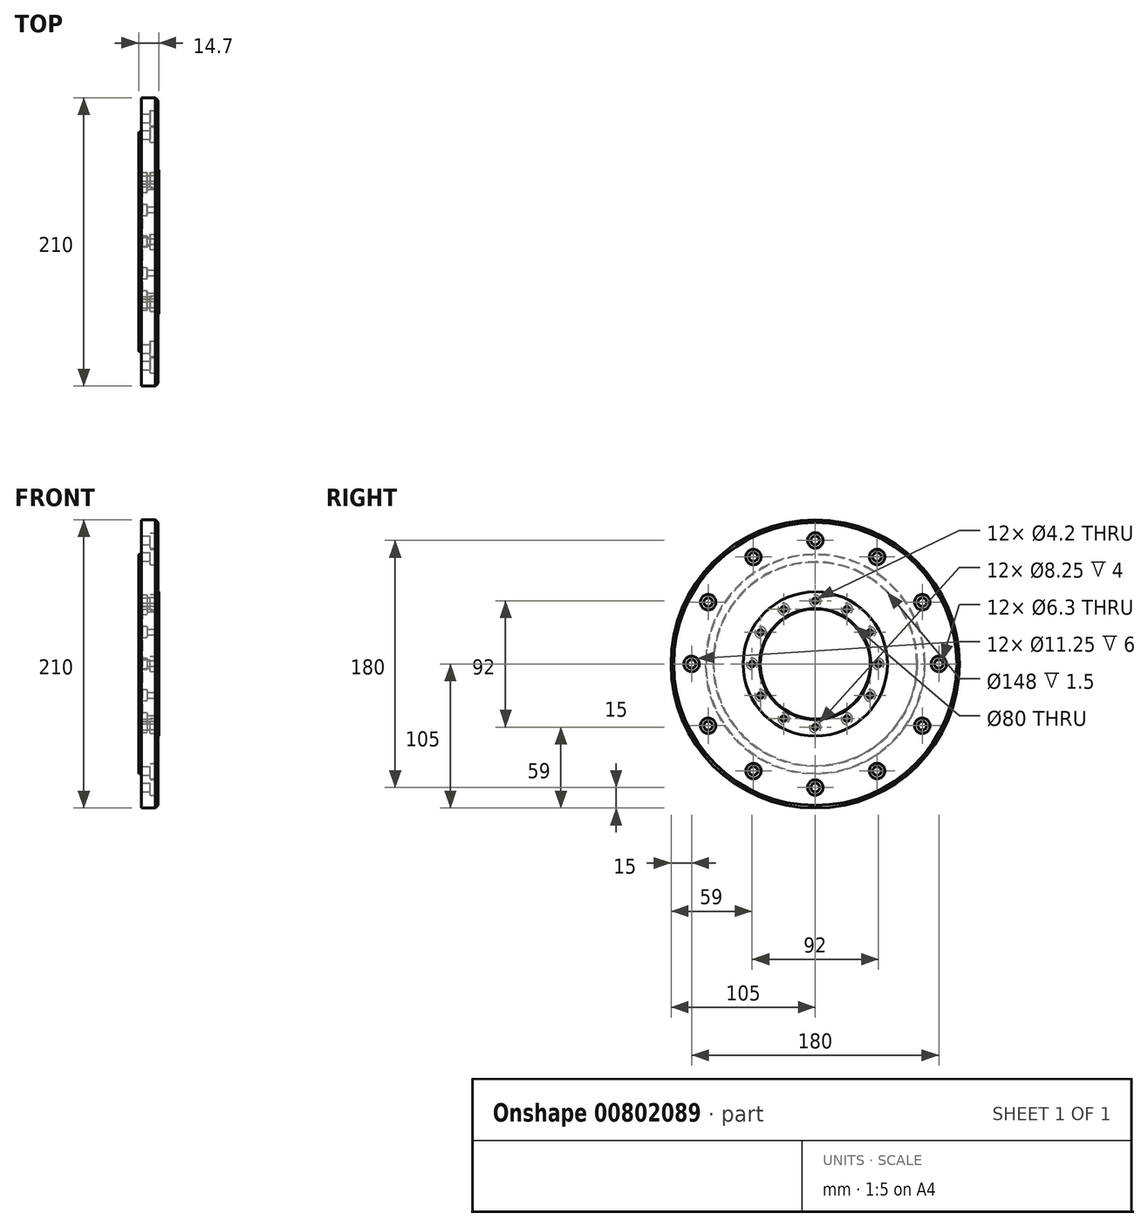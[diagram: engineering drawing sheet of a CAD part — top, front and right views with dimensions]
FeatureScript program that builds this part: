
annotation { "Feature Type Name" : "Feature", "Feature Type Description" : "" }
export const myFeature = defineFeature(function(context is Context, id is Id, definition is map)
    precondition{}
    {
        {
            var Q0;
            Q0=qCreatedBy(makeId("Front.planeOp"),FACE);
            var sketch = newSketch(context, id + "F0", { "sketchPlane" : qUnion([Q0])});
            skLineSegment(sketch, "E0", {"start": v(91.08, 0) * mm, "end": v(-135.26, 0) * mm, "construction": true});
            skLineSegment(sketch, "E1", {"start": v(-4.62, 80) * mm, "end": v(-4.62, 105) * mm});
            skLineSegment(sketch, "E2", {"start": v(-4.62, 105) * mm, "end": v(7.58, 105) * mm});
            skLineSegment(sketch, "E3", {"start": v(7.58, 105) * mm, "end": v(7.58, 52.5) * mm});
            skLineSegment(sketch, "E4", {"start": v(7.58, 52.5) * mm, "end": v(8.08, 52.5) * mm});
            skLineSegment(sketch, "E5", {"start": v(8.08, 52.5) * mm, "end": v(8.08, 40) * mm});
            skLineSegment(sketch, "E6", {"start": v(-4.62, 80) * mm, "end": v(-6.62, 80) * mm});
            skLineSegment(sketch, "E7", {"start": v(8.08, 40) * mm, "end": v(-4.62, 40) * mm});
            skLineSegment(sketch, "E8", {"start": v(-6.62, 80) * mm, "end": v(-6.62, 74) * mm});
            skLineSegment(sketch, "E9", {"start": v(-6.62, 74) * mm, "end": v(-4.62, 74) * mm});
            skLineSegment(sketch, "E10", {"start": v(-4.62, 74) * mm, "end": v(-4.62, 40) * mm});
            skPoint(sketch, "E11.orphan", {"position": v(-6.62, 40) * mm});
            skSolve(sketch);
        }
        {
            var Q0;
            Q0 = qSketchRegion(id + "F0", true);
            var Q1;
            Q1=sQuery(id+"F0.wireOp",EDGE,"E0");
            revolve(context, id + "F1", {"entities" : qUnion([Q0]), "axis" : qUnion([Q1]), "revolveType" : RevolveType.FULL});
        }
        {
            var Q0;
            Q0=makeQuery(id+"F1.opRevolve","SWEPT_FACE",FACE,{"disambiguationData":[OSD([sQuery(id+"F0.wireOp",EDGE,"E1")])]});
            var sketch = newSketch(context, id + "F2", { "sketchPlane" : qUnion([Q0])});
            skPoint(sketch, "E12", {"position": v(0, 0) * mm});
            skPoint(sketch, "E13", {"position": v(0, 46) * mm});
            skPoint(sketch, "E14", {"position": v(23, 39.84) * mm});
            skPoint(sketch, "E15", {"position": v(39.84, 23) * mm});
            skPoint(sketch, "E16", {"position": v(46, 0) * mm});
            skPoint(sketch, "E17", {"position": v(39.84, -23) * mm});
            skPoint(sketch, "E18", {"position": v(23, -39.84) * mm});
            skPoint(sketch, "E19", {"position": v(0, -46) * mm});
            skPoint(sketch, "E20", {"position": v(-23, -39.84) * mm});
            skPoint(sketch, "E21", {"position": v(-39.84, -23) * mm});
            skPoint(sketch, "E22", {"position": v(-46, 0) * mm});
            skPoint(sketch, "E23", {"position": v(-39.84, 23) * mm});
            skPoint(sketch, "E24", {"position": v(-23, 39.84) * mm});
            skSolve(sketch);
        }
        {
            var Q0;
            Q0=makeQuery(id+"F1.opRevolve","SWEPT_FACE",FACE,{"disambiguationData":[OSD([sQuery(id+"F0.wireOp",EDGE,"E3")])]});
            var sketch = newSketch(context, id + "F3", { "sketchPlane" : qUnion([Q0])});
            skPoint(sketch, "E25.center", {"position": v(0, 0) * mm});
            skPoint(sketch, "E26", {"position": v(0, 90) * mm});
            skPoint(sketch, "E27", {"position": v(45, 77.94) * mm});
            skPoint(sketch, "E28", {"position": v(77.94, 45) * mm});
            skPoint(sketch, "E29", {"position": v(90, 0) * mm});
            skPoint(sketch, "E30", {"position": v(77.94, -45) * mm});
            skPoint(sketch, "E31", {"position": v(45, -77.94) * mm});
            skPoint(sketch, "E32", {"position": v(0, -90) * mm});
            skPoint(sketch, "E33", {"position": v(-45, -77.94) * mm});
            skPoint(sketch, "E34", {"position": v(-77.94, -45) * mm});
            skPoint(sketch, "E35", {"position": v(-90, 0) * mm});
            skPoint(sketch, "E36", {"position": v(-77.94, 45) * mm});
            skPoint(sketch, "E37", {"position": v(-45, 77.94) * mm});
            skSolve(sketch);
        }
        {
            var Q0;
            Q0=sQuery(id+"F2.wireOp",VERTEX,"E13");
            var Q1;
            Q1=sQuery(id+"F2.wireOp",VERTEX,"E14");
            var Q2;
            Q2=sQuery(id+"F2.wireOp",VERTEX,"E15");
            var Q3;
            Q3=sQuery(id+"F2.wireOp",VERTEX,"E16");
            var Q4;
            Q4=sQuery(id+"F2.wireOp",VERTEX,"E17");
            var Q5;
            Q5=sQuery(id+"F2.wireOp",VERTEX,"E18");
            var Q6;
            Q6=sQuery(id+"F2.wireOp",VERTEX,"E19");
            var Q7;
            Q7=sQuery(id+"F2.wireOp",VERTEX,"E20");
            var Q8;
            Q8=sQuery(id+"F2.wireOp",VERTEX,"E22");
            var Q9;
            Q9=sQuery(id+"F2.wireOp",VERTEX,"E21");
            var Q10;
            Q10=sQuery(id+"F2.wireOp",VERTEX,"E23");
            var Q11;
            Q11=sQuery(id+"F2.wireOp",VERTEX,"E24");
            var Q12;
            Q12=makeQuery(id+"F1.opRevolve","SWEPT_BODY",BODY,{"disambiguationData":[OSD([sQuery(id+"F0.wireOp",EDGE,"8f36247e-526f-4479-acc4-7eec241f1e58"),sQuery(id+"F0.wireOp",EDGE,"E1"),sQuery(id+"F0.wireOp",EDGE,"E2"),sQuery(id+"F0.wireOp",EDGE,"E3"),sQuery(id+"F0.wireOp",EDGE,"E4"),sQuery(id+"F0.wireOp",EDGE,"E5")])]});
            hole(context, id + "F4", {"style" : HoleStyle.C_BORE, "endStyle" : HoleEndStyle.THROUGH, "standardTappedOrClearance" : lookupTablePath({ "standard" : "ISO", "fit" : "Close", "size" : "M4", "type" : "Clearance" }), "standardBlindInLast" : lookupTablePath({ "fit" : "Close", "standard" : "ISO", "size" : "M4", "type" : "Clearance" }), "holeDiameter" : 4.2 * mm, "cBoreDiameter" : 8.25 * mm, "cBoreDepth" : 4 * mm, "tappedDepth" : 16.82 * mm, "tapClearance" : 3, "startFromSketch" : true, "locations" : qUnion([Q0, Q1, Q2, Q3, Q4, Q5, Q6, Q7, Q8, Q9, Q10, Q11]), "scope" : qUnion([Q12])});
        }
        {
            var Q0;
            Q0=sQuery(id+"F3.wireOp",VERTEX,"E26");
            var Q1;
            Q1=sQuery(id+"F3.wireOp",VERTEX,"E27");
            var Q2;
            Q2=sQuery(id+"F3.wireOp",VERTEX,"E28");
            var Q3;
            Q3=sQuery(id+"F3.wireOp",VERTEX,"E29");
            var Q4;
            Q4=sQuery(id+"F3.wireOp",VERTEX,"E30");
            var Q5;
            Q5=sQuery(id+"F3.wireOp",VERTEX,"E31");
            var Q6;
            Q6=sQuery(id+"F3.wireOp",VERTEX,"E32");
            var Q7;
            Q7=sQuery(id+"F3.wireOp",VERTEX,"E33");
            var Q8;
            Q8=sQuery(id+"F3.wireOp",VERTEX,"E34");
            var Q9;
            Q9=sQuery(id+"F3.wireOp",VERTEX,"E35");
            var Q10;
            Q10=sQuery(id+"F3.wireOp",VERTEX,"E36");
            var Q11;
            Q11=sQuery(id+"F3.wireOp",VERTEX,"E37");
            var Q12;
            Q12=makeQuery(id+"F1.opRevolve","SWEPT_BODY",BODY,{"disambiguationData":[OSD([sQuery(id+"F0.wireOp",EDGE,"8f36247e-526f-4479-acc4-7eec241f1e58"),sQuery(id+"F0.wireOp",EDGE,"E1"),sQuery(id+"F0.wireOp",EDGE,"E2"),sQuery(id+"F0.wireOp",EDGE,"E3"),sQuery(id+"F0.wireOp",EDGE,"E4"),sQuery(id+"F0.wireOp",EDGE,"E5")])]});
            hole(context, id + "F5", {"style" : HoleStyle.C_BORE, "endStyle" : HoleEndStyle.THROUGH, "standardTappedOrClearance" : lookupTablePath({ "standard" : "ISO", "fit" : "Close", "size" : "M6", "type" : "Clearance" }), "standardBlindInLast" : lookupTablePath({ "fit" : "Close", "standard" : "ISO", "size" : "M6", "type" : "Clearance" }), "holeDiameter" : 6.3 * mm, "cBoreDiameter" : 11.25 * mm, "cBoreDepth" : 6 * mm, "tappedDepth" : 16.82 * mm, "tapClearance" : 3, "startFromSketch" : true, "locations" : qUnion([Q0, Q1, Q2, Q3, Q4, Q5, Q6, Q7, Q8, Q9, Q10, Q11]), "scope" : qUnion([Q12])});
        }
        {
            var Q0;
            Q0=makeQuery(id+"F1.opRevolve","SWEPT_EDGE",EDGE,{"disambiguationData":[OSD([sQuery(id+"F0.wireOp",EDGE,"E2"),sQuery(id+"F0.wireOp",EDGE,"E3")])]});
            chamfer(context, id + "F6", {"entities" : qUnion([Q0]), "width" : 2 * mm, "tangentPropagation" : true});
        }
        {
            var Q0;
            Q0=makeQuery(id+"F1.opRevolve","SWEPT_EDGE",EDGE,{"disambiguationData":[OSD([sQuery(id+"F0.wireOp",EDGE,"E6"),sQuery(id+"F0.wireOp",EDGE,"E8")])]});
            var Q1;
            Q1=makeQuery(id+"F1.opRevolve","SWEPT_EDGE",EDGE,{"disambiguationData":[OSD([sQuery(id+"F0.wireOp",EDGE,"E7"),sQuery(id+"F0.wireOp",EDGE,"E8")])]});
            chamfer(context, id + "F7", {"entities" : qUnion([Q0, Q1]), "width" : .5 * mm, "tangentPropagation" : true});
        }
    });
